# Revit family: Porta GSL dupla
name_source: partatom
category: Doors
units: mm (PartAtom-declared; Revit-internal decimal feet)

## family parameters
Cut with Voids When Loaded = Yes
Host = Face
Room Calculation Point = No
Shared = No

## types (2) — shared parameters
Define Thermal Properties by = Schematic Type
zero-valued in all types: Default Elevation

## per-type parameters (varying)
| type | Altura Vao Luz | Espessura Folha | Folha 32mm | Folha 50mm | Largura Vao Luz | Largura folha | Offset | Offset Dobradica |
| 32 - 800 x 2100 | 2100 mm | 32 mm  [stored 0.104987 ft] | Yes | No | 800 mm  [stored 2.62467 ft] | 382 mm | 45 mm  [stored 0.147638 ft] | 19 mm  [stored 0.062336 ft] |
| 50 - 1000 x 2100 | 2200 mm | 50 mm  [stored 0.164042 ft] | No | Yes | 2200 mm | 1082 mm | 58 mm | 20 mm  [stored 0.0656168 ft] |

note: [stored X ft] marks values corroborated as IEEE doubles in the binary element streams (Revit-internal decimal feet)

## geometry (parser evidence)
native form markers: Blend x2
no freeform markers — native parametric forms only
